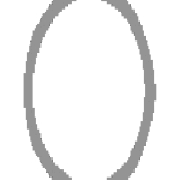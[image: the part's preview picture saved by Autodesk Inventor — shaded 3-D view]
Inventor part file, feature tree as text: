
AUTODESK INVENTOR PART (.ipt)
format: ipt  version: 2021 (Build 250183000, 183)  size: 109,056 bytes
history: native  units: in
note: dims shown in document units (in); Inventor stores cm internally (conversion verified against a paired STEP export)
features: other x4, sketch x3, plane x1
ambient origin geometry x8: Origin, YZ Plane, XZ Plane, XY Plane, X Axis, Y Axis, Z Axis, Center Point
bodies: Solid1 (feature_tree), Body (feature_tree)
feature tree (8):
  other  "Driven Length"
  other  "Frame Generator"
  other  "Start Plane"
  other  "End Plane"
  sketch  "Sketch"  dims[d2=28.1877in d4=-0.0in d5=28.1877in d6=0.12in d7=0.0in d8=90.0deg d9=28.1877in]
  sketch  "Sketch2"  dims[d0=1.0in]
  plane  "Work Plane3"
  sketch  "Sketch3"  dims[d1=0.065in]
